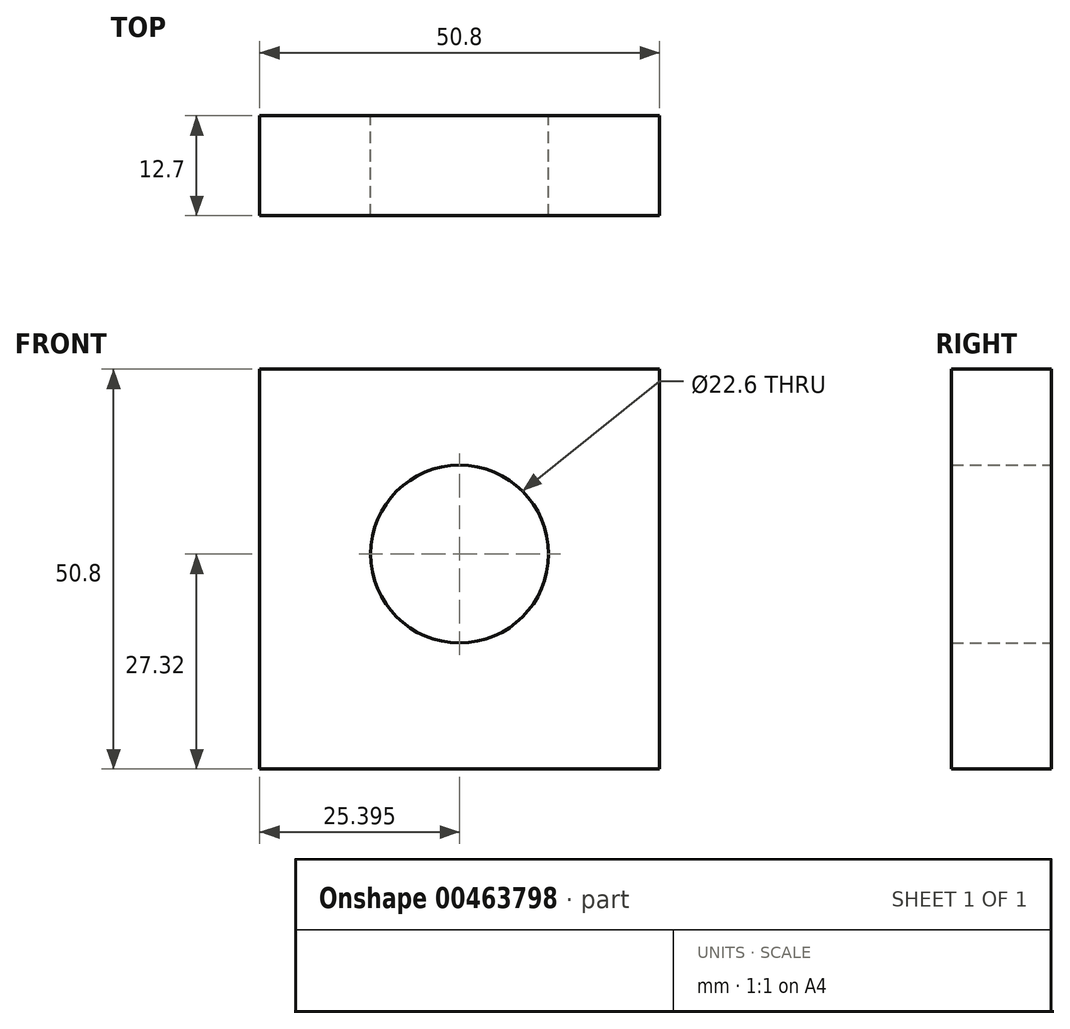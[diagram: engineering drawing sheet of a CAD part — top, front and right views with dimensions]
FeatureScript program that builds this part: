
annotation { "Feature Type Name" : "Feature", "Feature Type Description" : "" }
export const myFeature = defineFeature(function(context is Context, id is Id, definition is map)
    precondition{}
    {
        {
            var Q0;
            Q0=qCreatedBy(makeId("Front.planeOp"),FACE);
            var sketch = newSketch(context, id + "F0", { "sketchPlane" : qUnion([Q0])});
            skLineSegment(sketch, "E0.bottom", {"start": v(-18.95, 32.76) * mm, "end": v(31.85, 32.76) * mm});
            skLineSegment(sketch, "E0.top", {"start": v(-18.95, -18.04) * mm, "end": v(31.85, -18.04) * mm});
            skLineSegment(sketch, "E0.left", {"start": v(-18.95, 32.76) * mm, "end": v(-18.95, -18.04) * mm});
            skLineSegment(sketch, "E0.right", {"start": v(31.85, 32.76) * mm, "end": v(31.85, -18.04) * mm});
            skCircle(sketch, "E1", {"center": v(6.45, 9.28) * mm, "radius": 11.3 * mm});
            skPoint(sketch, "E1.centerSnap0", {"position": v(6.45, 32.76) * mm});
            skSolve(sketch);
        }
        {
            var Q0;
            Q0 = qSketchRegion(id + "F0", true);
            extrude(context, id + "F1", {"entities" : qUnion([Q0]), "depth" : 12.7 * mm});
        }
        {
            var Q0;
            Q0 = qSketchRegion(id + "F0", true);
            extrude(context, id + "F2", {"entities" : qUnion([Q0]), "operationType" : NewBodyOperationType.ADD, "depth" : 12.7 * mm});
        }
    });
